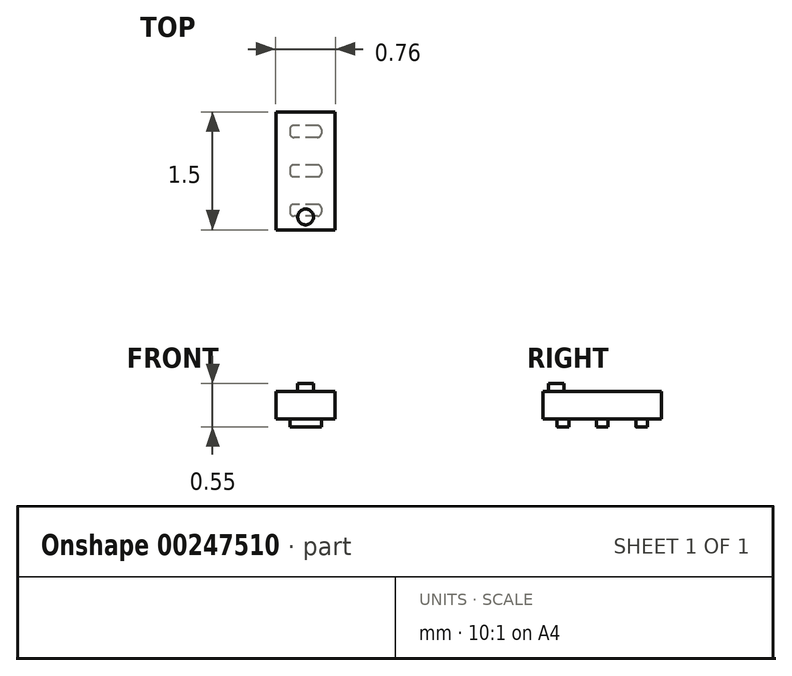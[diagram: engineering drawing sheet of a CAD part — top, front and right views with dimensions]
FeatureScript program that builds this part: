
annotation { "Feature Type Name" : "Feature", "Feature Type Description" : "" }
export const myFeature = defineFeature(function(context is Context, id is Id, definition is map)
    precondition{}
    {
        {
            var Q0;
            Q0=qCreatedBy(makeId("Top.planeOp"),FACE);
            var sketch = newSketch(context, id + "F0", { "sketchPlane" : qUnion([Q0])});
            skLineSegment(sketch, "E0.bottom", {"start": v(0.38, -0.75) * mm, "end": v(-0.37, -0.75) * mm});
            skLineSegment(sketch, "E0.top", {"start": v(0.37, 0.75) * mm, "end": v(-0.38, 0.75) * mm});
            skLineSegment(sketch, "E0.left", {"start": v(0.38, -0.75) * mm, "end": v(0.37, 0.75) * mm});
            skLineSegment(sketch, "E0.right", {"start": v(-0.37, -0.75) * mm, "end": v(-0.38, 0.75) * mm});
            skPoint(sketch, "E0.middle", {"position": v(0, 0) * mm});
            skSolve(sketch);
        }
        {
            var Q0;
            Q0 = qSketchRegion(id + "F0", true);
            extrude(context, id + "F1", {"entities" : qUnion([Q0]), "depth" : .35 * mm});
        }
        {
            var Q0;
            Q0=makeQuery(id+"F1.opExtrude","CAP_FACE",FACE,{"disambiguationData":[OSD([sQuery(id+"F0.wireOp",EDGE,"E0.bottom"),sQuery(id+"F0.wireOp",EDGE,"E0.top"),sQuery(id+"F0.wireOp",EDGE,"E0.left"),sQuery(id+"F0.wireOp",EDGE,"E0.right")])],"isStart":true});
            var sketch = newSketch(context, id + "F2", { "sketchPlane" : qUnion([Q0])});
            skSolve(sketch);
        }
        {
            var Q0;
            Q0=makeQuery(id+"F2.imprint","IMPRINT",FACE,{"disambiguationData":[TD([[makeQuery(id+"F2.imprint","IMPRINT",EDGE,{"derivedFrom":makeQuery(id+"F1.opExtrude","CAP_EDGE",EDGE,{"disambiguationData":[OSD([sQuery(id+"F0.wireOp",EDGE,"E0.bottom")])],"isStart":true})}),1.0]])]});
            var sketch = newSketch(context, id + "F3", { "sketchPlane" : qUnion([Q0])});
            skLineSegment(sketch, "E1", {"start": v(0, 0.75) * mm, "end": v(0, -0.75) * mm, "construction": true});
            skLineSegment(sketch, "E2.bottom", {"start": v(0.15, -0.07) * mm, "end": v(-0.15, -0.07) * mm});
            skLineSegment(sketch, "E2.top", {"start": v(0.15, 0.08) * mm, "end": v(-0.15, 0.07) * mm});
            skLineSegment(sketch, "E2.left", {"start": v(0.2, -0.02) * mm, "end": v(0.2, 0.03) * mm});
            skLineSegment(sketch, "E2.right", {"start": v(-0.2, -0.02) * mm, "end": v(-0.2, 0.02) * mm});
            skPoint(sketch, "E2.middle", {"position": v(0, 0) * mm});
            skPoint(sketch, "E3.visualSharp", {"position": v(-0.2, 0.07) * mm});
            skArc(sketch, "E3.filletArc", {"start": v(-0.15, 0.07) * mm, "mid": v(-0.19, 0.06) * mm, "end": v(-0.2, 0.02) * mm});
            skPoint(sketch, "E4.visualSharp", {"position": v(0.2, 0.08) * mm});
            skArc(sketch, "E4.filletArc", {"start": v(0.2, 0.03) * mm, "mid": v(0.19, 0.06) * mm, "end": v(0.15, 0.08) * mm});
            skPoint(sketch, "E5.visualSharp", {"position": v(0.2, -0.07) * mm});
            skArc(sketch, "E5.filletArc", {"start": v(0.15, -0.07) * mm, "mid": v(0.19, -0.06) * mm, "end": v(0.2, -0.02) * mm});
            skPoint(sketch, "E6.visualSharp", {"position": v(-0.2, -0.08) * mm});
            skArc(sketch, "E6.filletArc", {"start": v(-0.2, -0.03) * mm, "mid": v(-0.19, -0.06) * mm, "end": v(-0.15, -0.07) * mm});
            skLineSegment(sketch, "E7.bottom", {"start": v(0.15, 0.43) * mm, "end": v(-0.15, 0.43) * mm});
            skLineSegment(sketch, "E7.top", {"start": v(0.15, 0.57) * mm, "end": v(-0.15, 0.57) * mm});
            skLineSegment(sketch, "E7.left", {"start": v(0.2, 0.48) * mm, "end": v(0.2, 0.53) * mm});
            skLineSegment(sketch, "E7.right", {"start": v(-0.2, 0.48) * mm, "end": v(-0.2, 0.53) * mm});
            skPoint(sketch, "E7.middle", {"position": v(0, 0.5) * mm});
            skPoint(sketch, "E8.visualSharp", {"position": v(-0.2, 0.57) * mm});
            skArc(sketch, "E8.filletArc", {"start": v(-0.15, 0.57) * mm, "mid": v(-0.19, 0.56) * mm, "end": v(-0.2, 0.53) * mm});
            skPoint(sketch, "E9.visualSharp", {"position": v(0.2, 0.57) * mm});
            skArc(sketch, "E9.filletArc", {"start": v(0.2, 0.53) * mm, "mid": v(0.19, 0.56) * mm, "end": v(0.15, 0.57) * mm});
            skPoint(sketch, "E10.visualSharp", {"position": v(0.2, 0.43) * mm});
            skArc(sketch, "E10.filletArc", {"start": v(0.15, 0.43) * mm, "mid": v(0.19, 0.44) * mm, "end": v(0.2, 0.48) * mm});
            skPoint(sketch, "E11.visualSharp", {"position": v(-0.2, 0.43) * mm});
            skArc(sketch, "E11.filletArc", {"start": v(-0.2, 0.48) * mm, "mid": v(-0.19, 0.44) * mm, "end": v(-0.15, 0.43) * mm});
            skLineSegment(sketch, "E12.bottom", {"start": v(0.15, -0.57) * mm, "end": v(-0.15, -0.57) * mm});
            skLineSegment(sketch, "E12.top", {"start": v(0.15, -0.43) * mm, "end": v(-0.15, -0.43) * mm});
            skLineSegment(sketch, "E12.left", {"start": v(0.2, -0.53) * mm, "end": v(0.2, -0.48) * mm});
            skLineSegment(sketch, "E12.right", {"start": v(-0.2, -0.53) * mm, "end": v(-0.2, -0.48) * mm});
            skPoint(sketch, "E12.middle", {"position": v(0, -0.5) * mm});
            skPoint(sketch, "E13.visualSharp", {"position": v(-0.2, -0.42) * mm});
            skArc(sketch, "E13.filletArc", {"start": v(-0.15, -0.43) * mm, "mid": v(-0.19, -0.44) * mm, "end": v(-0.2, -0.48) * mm});
            skPoint(sketch, "E14.visualSharp", {"position": v(0.2, -0.43) * mm});
            skArc(sketch, "E14.filletArc", {"start": v(0.2, -0.48) * mm, "mid": v(0.19, -0.44) * mm, "end": v(0.15, -0.43) * mm});
            skPoint(sketch, "E15.visualSharp", {"position": v(0.2, -0.57) * mm});
            skArc(sketch, "E15.filletArc", {"start": v(0.15, -0.57) * mm, "mid": v(0.19, -0.56) * mm, "end": v(0.2, -0.53) * mm});
            skPoint(sketch, "E16.visualSharp", {"position": v(-0.2, -0.57) * mm});
            skArc(sketch, "E16.filletArc", {"start": v(-0.2, -0.53) * mm, "mid": v(-0.19, -0.56) * mm, "end": v(-0.15, -0.57) * mm});
            skSolve(sketch);
        }
        {
            var Q0;
            Q0 = qSketchRegion(id + "F3", true);
            extrude(context, id + "F4", {"entities" : qUnion([Q0]), "depth" : .1 * mm});
        }
        {
            var Q0;
            Q0=makeQuery(id+"F1.opExtrude","CAP_FACE",FACE,{"disambiguationData":[OSD([sQuery(id+"F0.wireOp",EDGE,"E0.bottom"),sQuery(id+"F0.wireOp",EDGE,"E0.top"),sQuery(id+"F0.wireOp",EDGE,"E0.left"),sQuery(id+"F0.wireOp",EDGE,"E0.right")])],"isStart":false});
            var sketch = newSketch(context, id + "F5", { "sketchPlane" : qUnion([Q0])});
            skCircle(sketch, "E17", {"center": v(0, -0.59) * mm, "radius": 0.1 * mm});
            skSolve(sketch);
        }
        {
            var Q0;
            Q0 = qSketchRegion(id + "F5", true);
            extrude(context, id + "F6", {"entities" : qUnion([Q0]), "depth" : .1 * mm});
        }
    });
